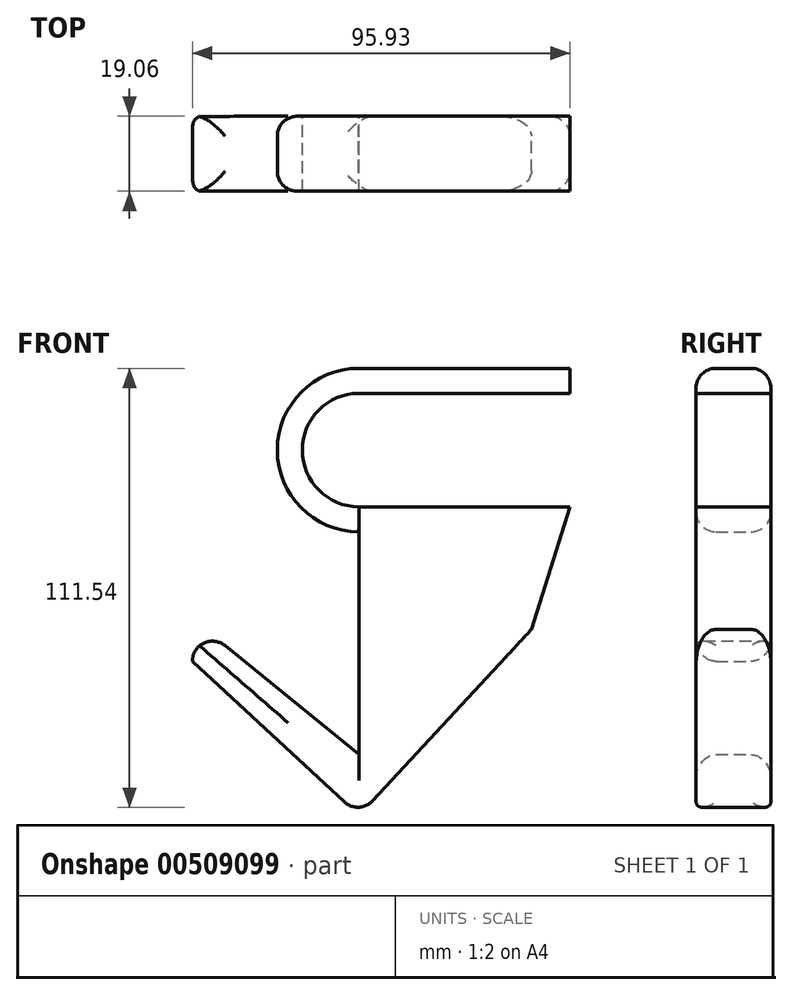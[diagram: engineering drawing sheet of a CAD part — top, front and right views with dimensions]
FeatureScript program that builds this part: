
annotation { "Feature Type Name" : "Feature", "Feature Type Description" : "" }
export const myFeature = defineFeature(function(context is Context, id is Id, definition is map)
    precondition{}
    {
        {
            var Q0;
            Q0=qCreatedBy(makeId("Front.planeOp"),FACE);
            var sketch = newSketch(context, id + "F0", { "sketchPlane" : qUnion([Q0])});
            skLineSegment(sketch, "E0", {"start": v(19.13, 38.52) * mm, "end": v(-34.47, 38.52) * mm});
            skLineSegment(sketch, "E1", {"start": v(-34.47, 9.68) * mm, "end": v(19.13, 9.68) * mm});
            skArc(sketch, "E2", {"start": v(-34.47, 38.52) * mm, "mid": v(-48.9, 24.1) * mm, "end": v(-34.47, 9.68) * mm});
            skLineSegment(sketch, "E3", {"start": v(19.13, 9.68) * mm, "end": v(9.32, -21.45) * mm});
            skLineSegment(sketch, "E4", {"start": v(9.32, -21.45) * mm, "end": v(-34.47, -21.45) * mm});
            skLineSegment(sketch, "E5", {"start": v(-34.47, -21.45) * mm, "end": v(-34.47, 9.68) * mm});
            skLineSegment(sketch, "E6", {"start": v(9.32, -21.45) * mm, "end": v(-34.47, -68.77) * mm});
            skLineSegment(sketch, "E7", {"start": v(-34.47, -68.77) * mm, "end": v(-34.47, -21.45) * mm});
            skLineSegment(sketch, "E8", {"start": v(-34.47, -68.77) * mm, "end": v(-76.8, -29.6) * mm});
            skLineSegment(sketch, "E9", {"start": v(-76.8, -29.6) * mm, "end": v(-76.8, -18.85) * mm});
            skLineSegment(sketch, "E10", {"start": v(-76.8, -18.85) * mm, "end": v(-34.47, -53.28) * mm});
            skArc(sketch, "E11.0", {"start": v(-34.47, 44.87) * mm, "mid": v(-55.25, 24.14) * mm, "end": v(-34.55, 3.33) * mm});
            skLineSegment(sketch, "E11.1", {"start": v(19.13, 44.87) * mm, "end": v(-34.47, 44.87) * mm});
            skLineSegment(sketch, "E12", {"start": v(19.13, 38.52) * mm, "end": v(19.13, 44.87) * mm});
            skLineSegment(sketch, "E13", {"start": v(-34.47, 9.68) * mm, "end": v(-34.55, 3.33) * mm});
            skLineSegment(sketch, "E14", {"start": v(-34.47, 0) * mm, "end": v(16.08, 0) * mm});
            skSolve(sketch);
        }
        {
            var Q0;
            Q0=makeQuery(id+"F0.imprint","IMPRINT",FACE,{"disambiguationData":[TD([[makeQuery(id+"F0.imprint","IMPRINT",EDGE,{"derivedFrom":sQuery(id+"F0.wireOp",EDGE,"E1")}),-1.0]])]});
            var Q1;
            {var subQ0=sQuery(id+"F0.wireOp",EDGE,"E4");Q1=makeQuery(id+"F0.imprint","IMPRINT",FACE,{"disambiguationData":[TD([[makeQuery(id+"F0.imprint","IMPRINT",EDGE,{"derivedFrom":subQ0}),1.0]])]});}
            var Q2;
            {var subQ0=sQuery(id+"F0.wireOp",EDGE,"E8");Q2=makeQuery(id+"F0.imprint","IMPRINT",FACE,{"disambiguationData":[TD([[makeQuery(id+"F0.imprint","IMPRINT",EDGE,{"derivedFrom":subQ0}),-1.0]])]});}
            var Q3;
            Q3=makeQuery(id+"F0.imprint","IMPRINT",FACE,{"disambiguationData":[TD([[makeQuery(id+"F0.imprint","IMPRINT",EDGE,{"derivedFrom":sQuery(id+"F0.wireOp",EDGE,"E0")}),-1.0]])]});
            var Q4;
            {var subQ0=sQuery(id+"F0.wireOp",EDGE,"E4");Q4=makeQuery(id+"F0.imprint","IMPRINT",FACE,{"disambiguationData":[TD([[makeQuery(id+"F0.imprint","IMPRINT",EDGE,{"derivedFrom":subQ0}),-1.0]])]});}
            extrude(context, id + "F1", {"entities" : qUnion([Q0, Q1, Q2, Q3, Q4]), "endBound" : BoundingType.SYMMETRIC, "depth" : 19.05 * mm});
        }
        {
            var Q0;
            Q0=makeQuery(id+"F1.opExtrude","CAP_EDGE",EDGE,{"disambiguationData":[OSD([sQuery(id+"F0.wireOp",EDGE,"E11.1")])],"isStart":false});
            var Q1;
            Q1=makeQuery(id+"F1.opExtrude","CAP_EDGE",EDGE,{"disambiguationData":[OSD([sQuery(id+"F0.wireOp",EDGE,"E11.1")])],"isStart":true});
            var Q2;
            Q2=makeQuery(id+"F1.opExtrude","CAP_EDGE",EDGE,{"disambiguationData":[OSD([sQuery(id+"F0.wireOp",EDGE,"E10")])],"isStart":false});
            var Q3;
            Q3=makeQuery(id+"F1.opExtrude","SWEPT_EDGE",EDGE,{"disambiguationData":[OSD([sQuery(id+"F0.wireOp",EDGE,"E9"),sQuery(id+"F0.wireOp",EDGE,"E10")])]});
            var Q4;
            Q4=makeQuery(id+"F1.opExtrude","CAP_EDGE",EDGE,{"disambiguationData":[OSD([sQuery(id+"F0.wireOp",EDGE,"E10")])],"isStart":true});
            var Q5;
            Q5=makeQuery(id+"F1.opExtrude","CAP_EDGE",EDGE,{"disambiguationData":[OSD([sQuery(id+"F0.wireOp",EDGE,"E3")])],"isStart":false});
            var Q6;
            Q6=makeQuery(id+"F1.opExtrude","CAP_EDGE",EDGE,{"disambiguationData":[OSD([sQuery(id+"F0.wireOp",EDGE,"E3")])],"isStart":true});
            fillet(context, id + "F2", {"entities" : qUnion([Q0, Q1, Q2, Q3, Q4, Q5, Q6]), "radius" : 5.08 * mm, "tangentPropagation" : true, "allowEdgeOverflow" : false});
        }
        {
            var Q0;
            {var subQ0=sQuery(id+"F0.wireOp",EDGE,"E9");Q0=makeQuery(id+"F2.opFillet","BLEND_EDGE",EDGE,{"blendedFrom":[makeQuery(id+"F1.opExtrude","SWEPT_EDGE",EDGE,{"disambiguationData":[OSD([subQ0,sQuery(id+"F0.wireOp",EDGE,"E10")])]}),makeQuery(id+"F1.opExtrude","SWEPT_FACE",FACE,{"disambiguationData":[OSD([subQ0])]})],"blendedInto":[makeQuery(id+"F1.opExtrude","SWEPT_FACE",FACE,{"disambiguationData":[OSD([subQ0])]})]});}
            var Q1;
            Q1=makeQuery(id+"F1.opExtrude","SWEPT_EDGE",EDGE,{"disambiguationData":[OSD([sQuery(id+"F0.wireOp",EDGE,"E6"),sQuery(id+"F0.wireOp",EDGE,"E7"),sQuery(id+"F0.wireOp",EDGE,"E8")])]});
            var Q2;
            Q2=makeQuery(id+"F1.opExtrude","CAP_EDGE",EDGE,{"disambiguationData":[OSD([sQuery(id+"F0.wireOp",EDGE,"E8")])],"isStart":false});
            var Q3;
            Q3=makeQuery(id+"F1.opExtrude","CAP_EDGE",EDGE,{"disambiguationData":[OSD([sQuery(id+"F0.wireOp",EDGE,"E8")])],"isStart":true});
            fillet(context, id + "F3", {"entities" : qUnion([Q0, Q1, Q2, Q3]), "radius" : 5.08 * mm, "tangentPropagation" : true, "allowEdgeOverflow" : false});
        }
    });
